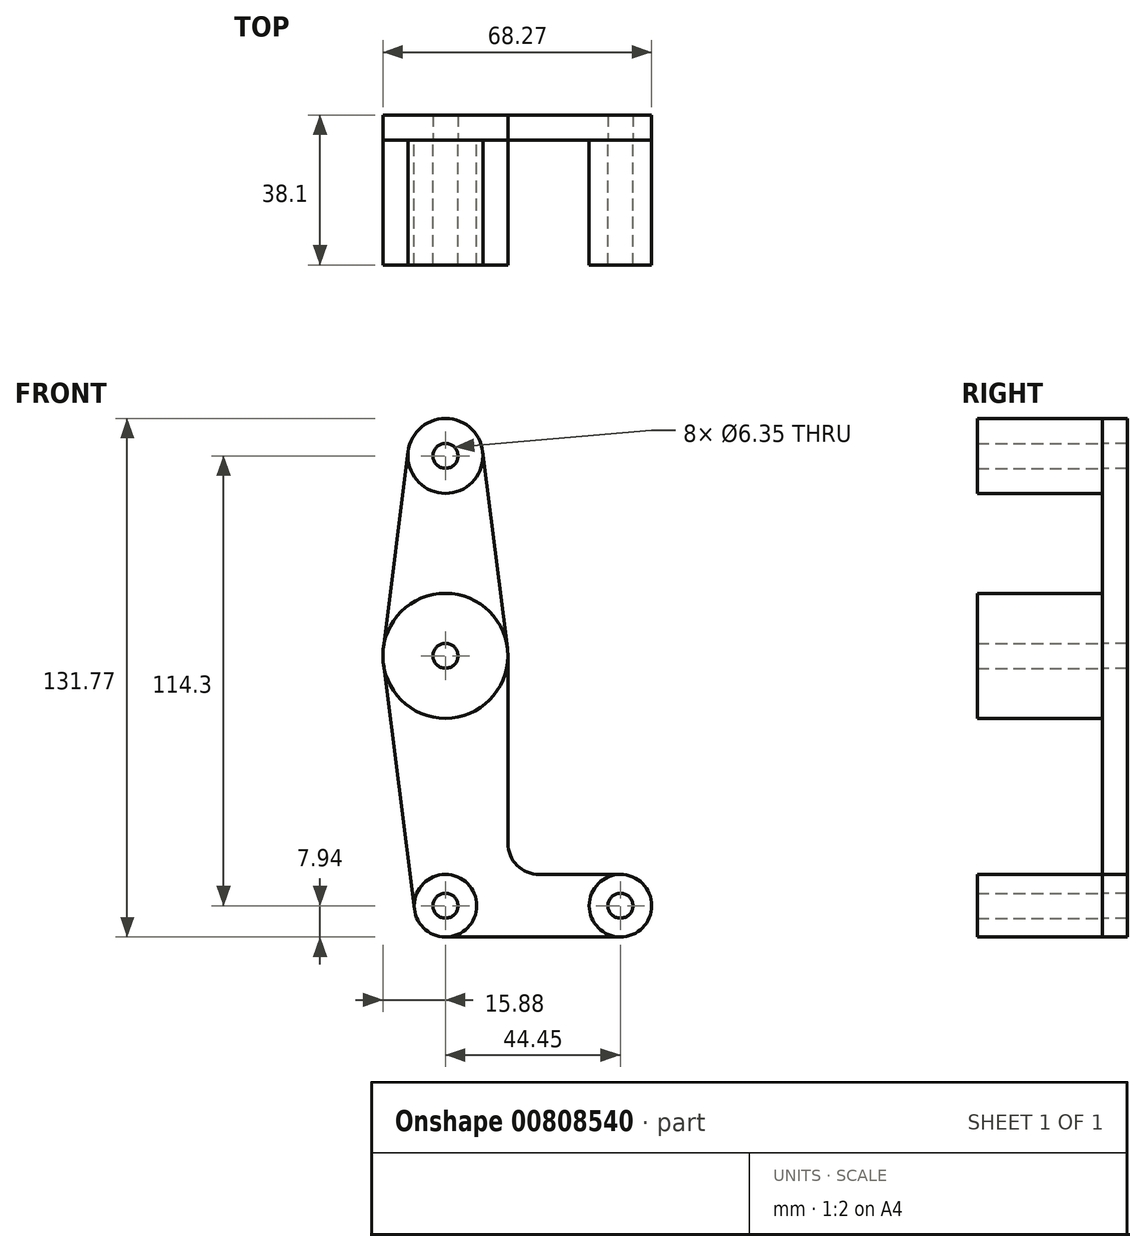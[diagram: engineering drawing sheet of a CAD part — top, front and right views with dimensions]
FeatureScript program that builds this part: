
annotation { "Feature Type Name" : "Feature", "Feature Type Description" : "" }
export const myFeature = defineFeature(function(context is Context, id is Id, definition is map)
    precondition{}
    {
        {
            var Q0;
            Q0=qCreatedBy(makeId("Front.planeOp"),FACE);
            var sketch = newSketch(context, id + "F0", { "sketchPlane" : qUnion([Q0])});
            skCircle(sketch, "E0", {"center": v(0, 0) * mm, "radius": 15.88 * mm});
            skCircle(sketch, "E1", {"center": v(0, 0) * mm, "radius": 3.18 * mm});
            skCircle(sketch, "E2", {"center": v(0, 50.8) * mm, "radius": 9.53 * mm});
            skCircle(sketch, "E3", {"center": v(0, 50.8) * mm, "radius": 3.18 * mm});
            skCircle(sketch, "E4", {"center": v(0, -63.5) * mm, "radius": 7.94 * mm});
            skCircle(sketch, "E5", {"center": v(0, -63.5) * mm, "radius": 3.18 * mm});
            skLineSegment(sketch, "E6", {"start": v(15.75, 1.98) * mm, "end": v(9.45, 52) * mm});
            skLineSegment(sketch, "E7", {"start": v(-15.75, 1.98) * mm, "end": v(-9.45, 52) * mm});
            skLineSegment(sketch, "E8", {"start": v(-7.88, -64.5) * mm, "end": v(-15.75, -1.98) * mm});
            skLineSegment(sketch, "E9", {"start": v(15.88, -47.62) * mm, "end": v(15.88, 0) * mm});
            skCircle(sketch, "E10", {"center": v(44.45, -63.5) * mm, "radius": 7.94 * mm});
            skLineSegment(sketch, "E11", {"start": v(44.45, -71.44) * mm, "end": v(0, -71.44) * mm});
            skLineSegment(sketch, "E12", {"start": v(44.45, -55.56) * mm, "end": v(23.81, -55.56) * mm});
            skCircle(sketch, "E13", {"center": v(44.45, -63.5) * mm, "radius": 3.18 * mm});
            skPoint(sketch, "E14.orphan", {"position": v(7.9, -64.3) * mm});
            skPoint(sketch, "E15.visualSharp", {"position": v(15.88, -55.56) * mm});
            skArc(sketch, "E15.filletArc", {"start": v(15.88, -47.62) * mm, "mid": v(18.2, -53.24) * mm, "end": v(23.81, -55.56) * mm});
            skSolve(sketch);
        }
        {
            var Q0;
            Q0=makeQuery(id+"F0.imprint","IMPRINT",FACE,{"disambiguationData":[TD([[makeQuery(id+"F0.imprint","IMPRINT",EDGE,{"derivedFrom":sQuery(id+"F0.wireOp",EDGE,"E3")}),-1.0]])]});
            var Q1;
            Q1=makeQuery(id+"F0.imprint","IMPRINT",FACE,{"disambiguationData":[TD([[makeQuery(id+"F0.imprint","IMPRINT",EDGE,{"derivedFrom":sQuery(id+"F0.wireOp",EDGE,"E5")}),-1.0]])]});
            var Q2;
            Q2=makeQuery(id+"F0.imprint","IMPRINT",FACE,{"disambiguationData":[TD([[makeQuery(id+"F0.imprint","IMPRINT",EDGE,{"derivedFrom":sQuery(id+"F0.wireOp",EDGE,"E13")}),-1.0]])]});
            var Q3;
            Q3=makeQuery(id+"F0.imprint","IMPRINT",FACE,{"disambiguationData":[TD([[makeQuery(id+"F0.imprint","IMPRINT",EDGE,{"derivedFrom":sQuery(id+"F0.wireOp",EDGE,"E1")}),-1.0]])]});
            extrude(context, id + "F1", {"entities" : qUnion([Q0, Q1, Q2, Q3]), "depth" : 31.75 * mm, "offsetDistance" : 25.4 * mm});
        }
        {
            var Q0;
            Q0=makeQuery(id+"F0.imprint","IMPRINT",FACE,{"disambiguationData":[TD([[makeQuery(id+"F0.imprint","IMPRINT",EDGE,{"derivedFrom":sQuery(id+"F0.wireOp",EDGE,"E3")}),-1.0]])]});
            var Q1;
            {var subQ0=sQuery(id+"F0.wireOp",EDGE,"E6");Q1=makeQuery(id+"F0.imprint","IMPRINT",FACE,{"disambiguationData":[TD([[makeQuery(id+"F0.imprint","IMPRINT",EDGE,{"derivedFrom":subQ0}),1.0]])]});}
            var Q2;
            Q2=makeQuery(id+"F0.imprint","IMPRINT",FACE,{"disambiguationData":[TD([[makeQuery(id+"F0.imprint","IMPRINT",EDGE,{"derivedFrom":sQuery(id+"F0.wireOp",EDGE,"E1")}),-1.0]])]});
            var Q3;
            {var subQ1=sQuery(id+"F0.wireOp",EDGE,"E8");Q3=makeQuery(id+"F0.imprint","IMPRINT",FACE,{"disambiguationData":[TD([[makeQuery(id+"F0.imprint","IMPRINT",EDGE,{"derivedFrom":subQ1}),-1.0]])]});}
            var Q4;
            Q4=makeQuery(id+"F0.imprint","IMPRINT",FACE,{"disambiguationData":[TD([[makeQuery(id+"F0.imprint","IMPRINT",EDGE,{"derivedFrom":sQuery(id+"F0.wireOp",EDGE,"E5")}),-1.0]])]});
            var Q5;
            Q5=makeQuery(id+"F0.imprint","IMPRINT",FACE,{"disambiguationData":[TD([[makeQuery(id+"F0.imprint","IMPRINT",EDGE,{"derivedFrom":sQuery(id+"F0.wireOp",EDGE,"E13")}),-1.0]])]});
            extrude(context, id + "F2", {"entities" : qUnion([Q0, Q1, Q2, Q3, Q4, Q5]), "oppositeDirection" : true, "depth" : 6.35 * mm, "offsetDistance" : 25.4 * mm});
        }
    });
